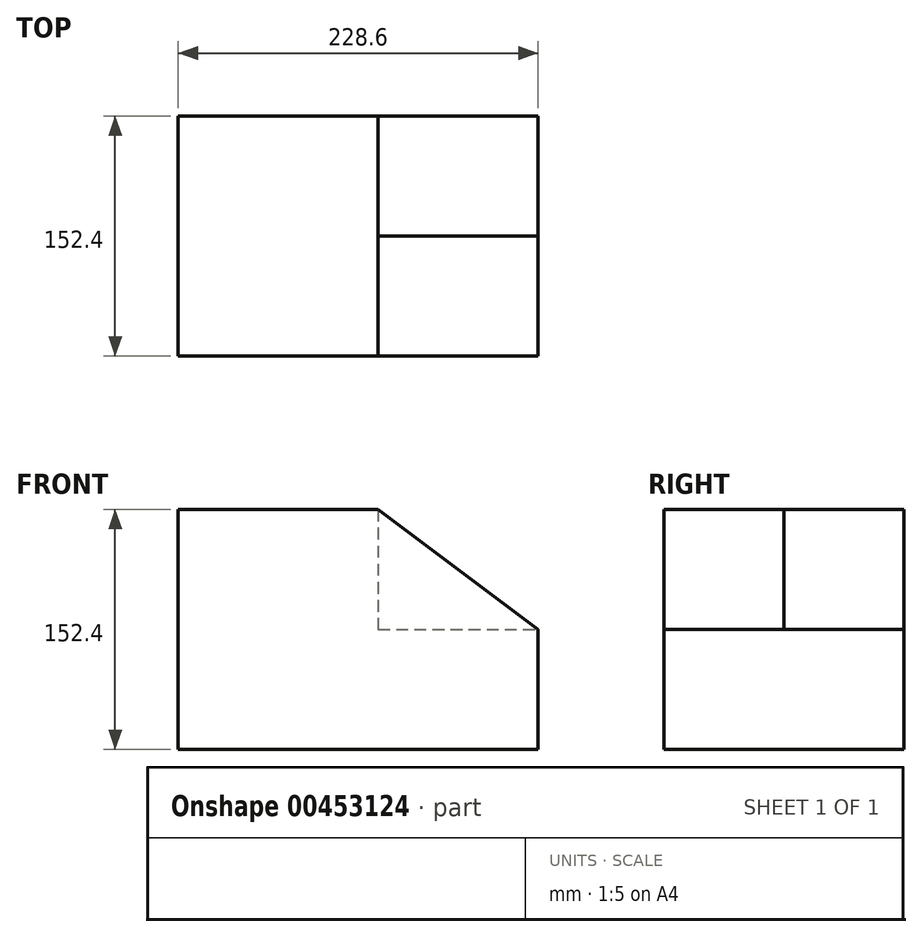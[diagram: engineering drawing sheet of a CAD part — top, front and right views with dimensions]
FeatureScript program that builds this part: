
annotation { "Feature Type Name" : "Feature", "Feature Type Description" : "" }
export const myFeature = defineFeature(function(context is Context, id is Id, definition is map)
    precondition{}
    {
        {
            var Q0;
            Q0=qCreatedBy(makeId("Front.planeOp"),FACE);
            var sketch = newSketch(context, id + "F0", { "sketchPlane" : qUnion([Q0])});
            skLineSegment(sketch, "E0", {"start": v(114.3, -76.2) * mm, "end": v(-114.3, -76.2) * mm});
            skLineSegment(sketch, "E1", {"start": v(-114.3, -76.2) * mm, "end": v(-114.3, 76.2) * mm});
            skLineSegment(sketch, "E2", {"start": v(-114.3, 76.2) * mm, "end": v(114.3, 76.2) * mm});
            skLineSegment(sketch, "E3", {"start": v(114.3, 76.2) * mm, "end": v(114.3, -76.2) * mm});
            skSolve(sketch);
        }
        {
            var Q0;
            Q0 = qSketchRegion(id + "F0", true);
            extrude(context, id + "F1", {"entities" : qUnion([Q0]), "endBound" : BoundingType.SYMMETRIC, "depth" : 152.4 * mm});
        }
        {
            var Q0;
            Q0=makeQuery(id+"F1.opExtrude","CAP_FACE",FACE,{"disambiguationData":[OSD([sQuery(id+"F0.wireOp",EDGE,"E0"),sQuery(id+"F0.wireOp",EDGE,"E1"),sQuery(id+"F0.wireOp",EDGE,"E2"),sQuery(id+"F0.wireOp",EDGE,"E3")])],"isStart":true});
            var sketch = newSketch(context, id + "F2", { "sketchPlane" : qUnion([Q0])});
            skLineSegment(sketch, "E4", {"start": v(114.3, 76.2) * mm, "end": v(12.7, 76.2) * mm});
            skLineSegment(sketch, "E5", {"start": v(12.7, 76.2) * mm, "end": v(114.3, 0) * mm});
            skLineSegment(sketch, "E6", {"start": v(114.3, 0) * mm, "end": v(114.3, 76.2) * mm});
            skLineSegment(sketch, "E7.MirrorCS", {"start": v(-12.7, 76.2) * mm, "end": v(-114.3, 0) * mm});
            skLineSegment(sketch, "E8.MirrorCS", {"start": v(-114.3, 0) * mm, "end": v(-114.3, 76.2) * mm});
            skLineSegment(sketch, "E9.MirrorCS", {"start": v(-114.3, 76.2) * mm, "end": v(-12.7, 76.2) * mm});
            skSolve(sketch);
        }
        {
            var Q0;
            Q0=makeQuery(id+"F2.imprint","IMPRINT",FACE,{"disambiguationData":[TD([[makeQuery(id+"F2.imprint","IMPRINT",EDGE,{"derivedFrom":sQuery(id+"F2.wireOp",EDGE,"E7.MirrorCS")}),-1.0]])]});
            extrude(context, id + "F3", {"entities" : qUnion([Q0]), "operationType" : NewBodyOperationType.REMOVE, "endBound" : BoundingType.THROUGH_ALL, "oppositeDirection" : true, "depth" : 25.4 * mm});
        }
        {
            var Q0;
            Q0=makeQuery(id+"F1.opExtrude","CAP_FACE",FACE,{"disambiguationData":[OSD([sQuery(id+"F0.wireOp",EDGE,"E0"),sQuery(id+"F0.wireOp",EDGE,"E1"),sQuery(id+"F0.wireOp",EDGE,"E2"),sQuery(id+"F0.wireOp",EDGE,"E3")])],"isStart":true});
            var sketch = newSketch(context, id + "F4", { "sketchPlane" : qUnion([Q0])});
            skLineSegment(sketch, "E10", {"start": v(-12.7, 76.2) * mm, "end": v(-12.7, 0) * mm});
            skLineSegment(sketch, "E11", {"start": v(-12.7, 0) * mm, "end": v(-114.3, 0) * mm});
            skLineSegment(sketch, "E12", {"start": v(-114.3, 0) * mm, "end": v(-12.7, 76.2) * mm});
            skSolve(sketch);
        }
        {
            var Q0;
            Q0=makeQuery(id+"F4.imprint","IMPRINT",FACE,{"disambiguationData":[TD([[makeQuery(id+"F4.imprint","IMPRINT",EDGE,{"derivedFrom":sQuery(id+"F4.wireOp",EDGE,"E10")}),-1.0]])]});
            extrude(context, id + "F5", {"entities" : qUnion([Q0]), "operationType" : NewBodyOperationType.REMOVE, "oppositeDirection" : true, "depth" : 76.2 * mm});
        }
    });
